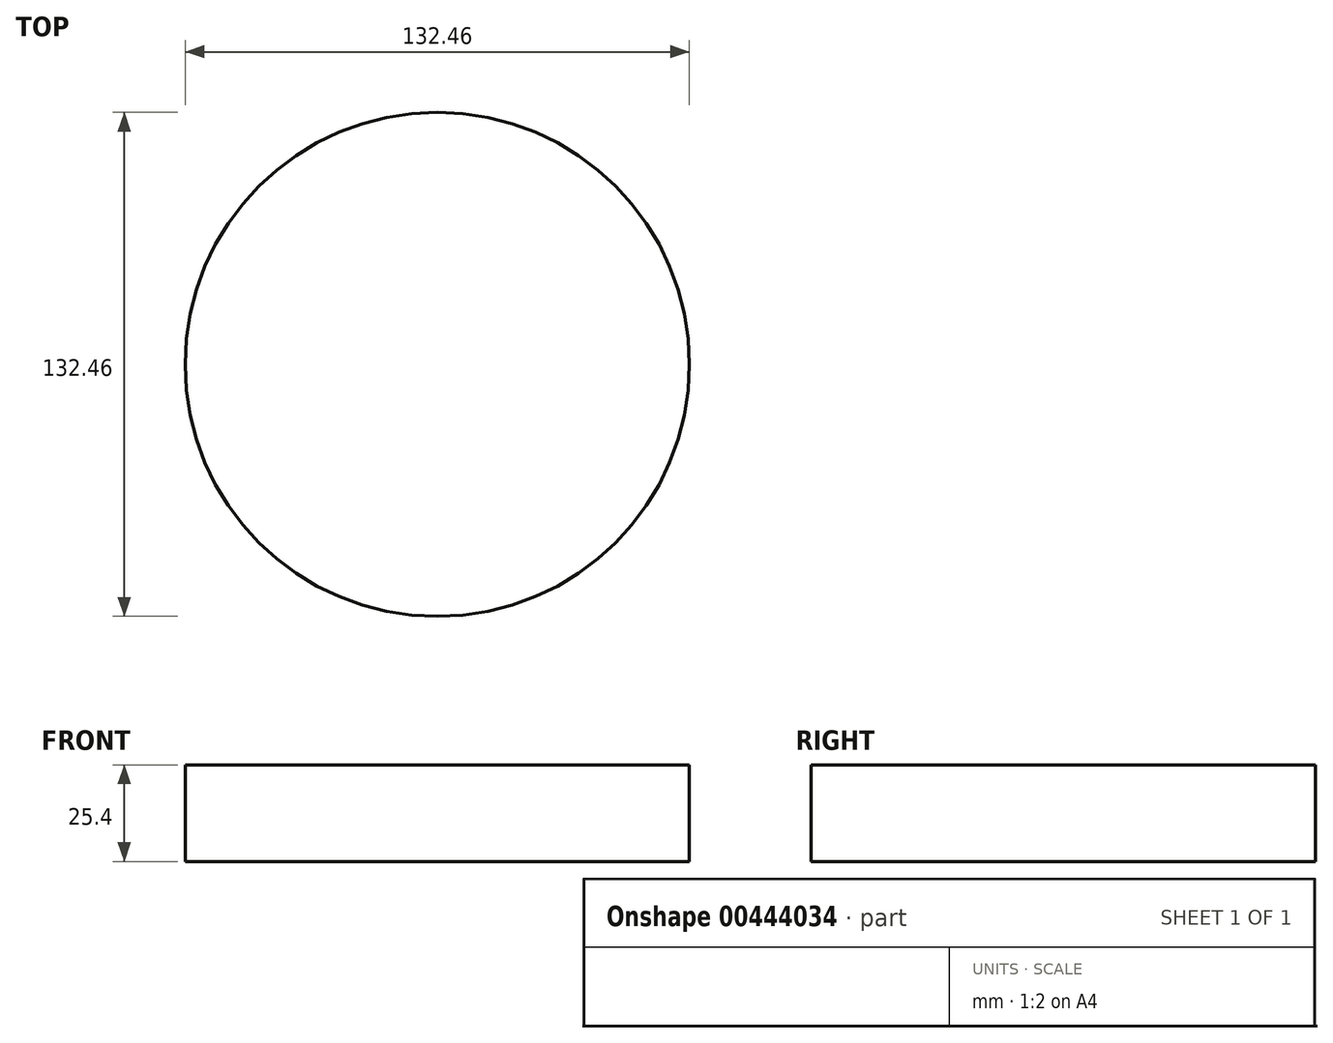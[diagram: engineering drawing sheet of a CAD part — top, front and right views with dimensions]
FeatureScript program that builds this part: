
annotation { "Feature Type Name" : "Feature", "Feature Type Description" : "" }
export const myFeature = defineFeature(function(context is Context, id is Id, definition is map)
    precondition{}
    {
        {
            var Q0;
            Q0=qCreatedBy(makeId("Top.planeOp"),FACE);
            var sketch = newSketch(context, id + "F0", { "sketchPlane" : qUnion([Q0])});
            skCircle(sketch, "E0", {"center": v(0, 0) * mm, "radius": 66.23 * mm});
            skSolve(sketch);
        }
        {
            var Q0;
            Q0 = qSketchRegion(id + "F0", true);
            extrude(context, id + "F1", {"entities" : qUnion([Q0]), "depth" : 25.4 * mm});
        }
    });
